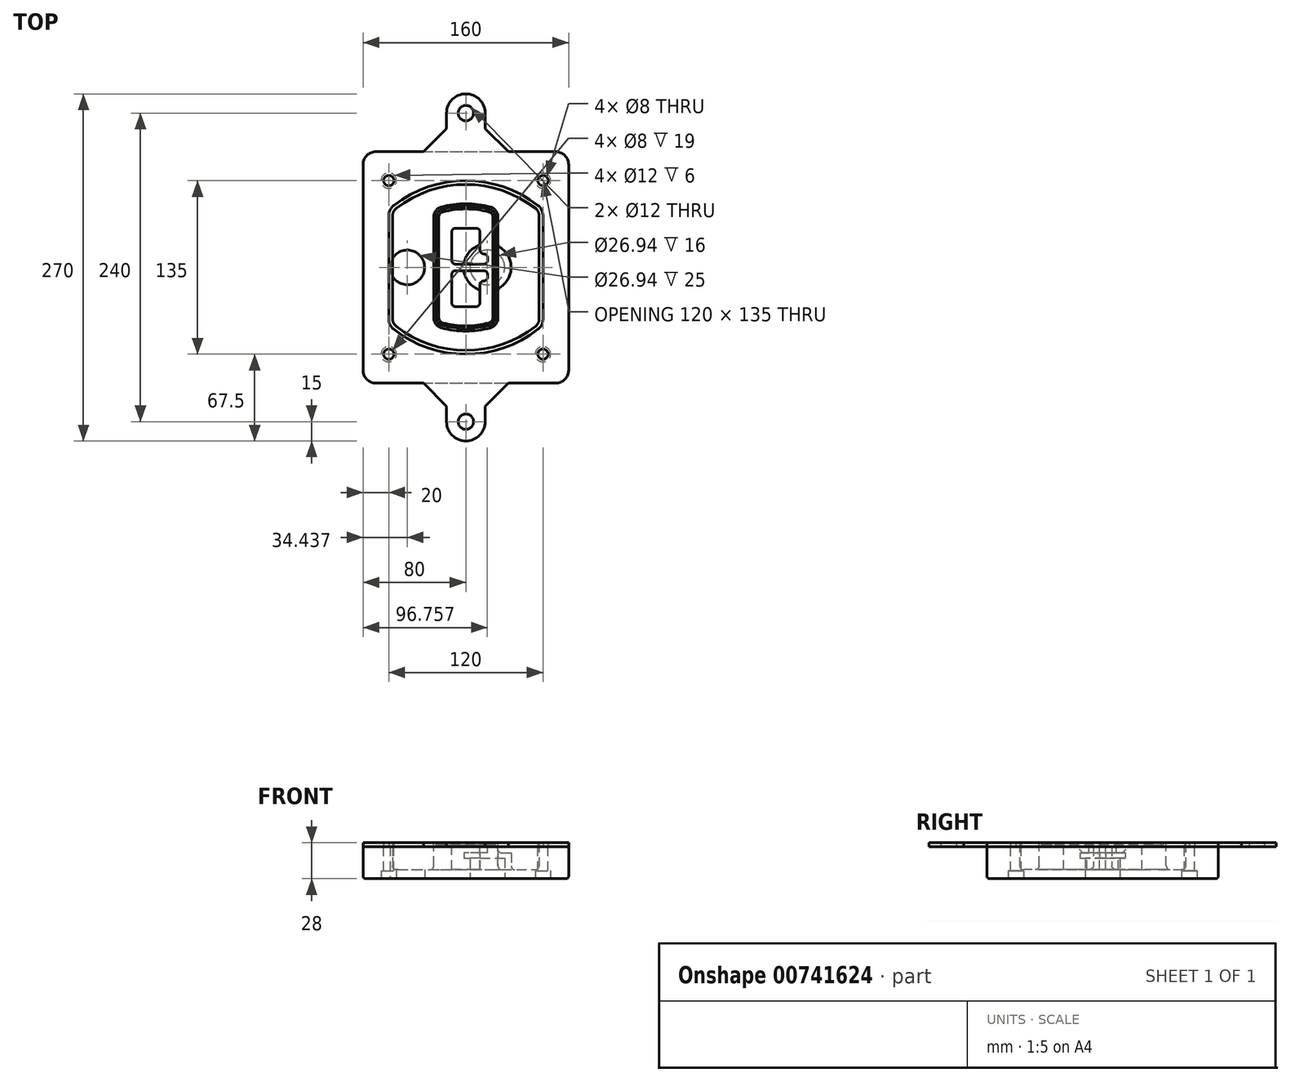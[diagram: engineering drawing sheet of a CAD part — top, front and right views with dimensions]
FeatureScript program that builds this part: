
annotation { "Feature Type Name" : "Feature", "Feature Type Description" : "" }
export const myFeature = defineFeature(function(context is Context, id is Id, definition is map)
    precondition{}
    {
        {
            var Q0;
            Q0=qCreatedBy(makeId("Top.planeOp"),FACE);
            var sketch = newSketch(context, id + "F0", { "sketchPlane" : qUnion([Q0])});
            skPoint(sketch, "E0.rect.middle", {"position": v(0, 0) * mm});
            skLineSegment(sketch, "E1.bottom", {"start": v(-70, -90) * mm, "end": v(70, -90) * mm});
            skLineSegment(sketch, "E1.top", {"start": v(-70, 90) * mm, "end": v(70, 90) * mm});
            skLineSegment(sketch, "E1.left", {"start": v(-80, -80) * mm, "end": v(-80, 80) * mm});
            skLineSegment(sketch, "E1.right", {"start": v(80, -80) * mm, "end": v(80, 80) * mm});
            skLineSegment(sketch, "E2", {"start": v(-80, 90) * mm, "end": v(80, -90) * mm, "construction": true});
            skLineSegment(sketch, "E3", {"start": v(80, 90) * mm, "end": v(-80, -90) * mm, "construction": true});
            skCircle(sketch, "E4", {"center": v(-60, 67.5) * mm, "radius": 4 * mm});
            skCircle(sketch, "E5", {"center": v(60, 67.5) * mm, "radius": 4 * mm});
            skCircle(sketch, "E6", {"center": v(60, -67.5) * mm, "radius": 4 * mm});
            skCircle(sketch, "E7", {"center": v(-60, -67.5) * mm, "radius": 4 * mm});
            skLineSegment(sketch, "E8", {"start": v(-60, 67.5) * mm, "end": v(60, 67.5) * mm, "construction": true});
            skLineSegment(sketch, "E9", {"start": v(60, 67.5) * mm, "end": v(60, -67.5) * mm, "construction": true});
            skLineSegment(sketch, "E10", {"start": v(60, -67.5) * mm, "end": v(-60, -67.5) * mm, "construction": true});
            skLineSegment(sketch, "E11", {"start": v(-60, -67.5) * mm, "end": v(-60, 67.5) * mm, "construction": true});
            skLineSegment(sketch, "E12", {"start": v(-60, 40.3) * mm, "end": v(-60, -40.3) * mm});
            skLineSegment(sketch, "E13", {"start": v(60, 40.3) * mm, "end": v(60, -40.3) * mm});
            skArc(sketch, "E14", {"start": v(56.15, 48.18) * mm, "mid": v(0, 67.5) * mm, "end": v(-56.15, 48.18) * mm});
            skArc(sketch, "E15", {"start": v(-56.15, -48.18) * mm, "mid": v(0, -67.5) * mm, "end": v(56.15, -48.18) * mm});
            skLineSegment(sketch, "E16", {"start": v(-60, 0) * mm, "end": v(60, 0) * mm, "construction": true});
            skPoint(sketch, "E17.visualSharp", {"position": v(-60, -45) * mm});
            skArc(sketch, "E17.filletArc", {"start": v(-60, -40.3) * mm, "mid": v(-58.99, -44.68) * mm, "end": v(-56.15, -48.18) * mm});
            skPoint(sketch, "E18.visualSharp", {"position": v(-60, 45) * mm});
            skArc(sketch, "E18.filletArc", {"start": v(-56.15, 48.18) * mm, "mid": v(-58.99, 44.68) * mm, "end": v(-60, 40.3) * mm});
            skPoint(sketch, "E19.visualSharp", {"position": v(60, 45) * mm});
            skArc(sketch, "E19.filletArc", {"start": v(60, 40.3) * mm, "mid": v(58.99, 44.68) * mm, "end": v(56.15, 48.18) * mm});
            skPoint(sketch, "E20.visualSharp", {"position": v(60, -45) * mm});
            skArc(sketch, "E20.filletArc", {"start": v(56.15, -48.18) * mm, "mid": v(58.99, -44.68) * mm, "end": v(60, -40.3) * mm});
            skPoint(sketch, "E21.visualSharp", {"position": v(-80, 90) * mm});
            skArc(sketch, "E21.filletArc", {"start": v(-70, 90) * mm, "mid": v(-77.07, 87.07) * mm, "end": v(-80, 80) * mm});
            skPoint(sketch, "E22.visualSharp", {"position": v(80, 90) * mm});
            skArc(sketch, "E22.filletArc", {"start": v(80, 80) * mm, "mid": v(77.07, 87.07) * mm, "end": v(70, 90) * mm});
            skPoint(sketch, "E23.visualSharp", {"position": v(80, -90) * mm});
            skArc(sketch, "E23.filletArc", {"start": v(70, -90) * mm, "mid": v(77.07, -87.07) * mm, "end": v(80, -80) * mm});
            skPoint(sketch, "E24.visualSharp", {"position": v(-80, -90) * mm});
            skArc(sketch, "E24.filletArc", {"start": v(-80, -80) * mm, "mid": v(-77.07, -87.07) * mm, "end": v(-70, -90) * mm});
            skArc(sketch, "E25.0", {"start": v(57, 40.3) * mm, "mid": v(56.3, 43.36) * mm, "end": v(54.3, 45.81) * mm});
            skLineSegment(sketch, "E25.1", {"start": v(57, 40.3) * mm, "end": v(57, -40.3) * mm});
            skArc(sketch, "E25.2", {"start": v(54.3, -45.81) * mm, "mid": v(56.3, -43.36) * mm, "end": v(57, -40.3) * mm});
            skArc(sketch, "E25.3", {"start": v(-54.3, -45.81) * mm, "mid": v(0, -64.5) * mm, "end": v(54.3, -45.81) * mm});
            skArc(sketch, "E25.4", {"start": v(-57, -40.3) * mm, "mid": v(-56.3, -43.36) * mm, "end": v(-54.3, -45.81) * mm});
            skArc(sketch, "E25.5", {"start": v(54.3, 45.81) * mm, "mid": v(0, 64.5) * mm, "end": v(-54.3, 45.81) * mm});
            skLineSegment(sketch, "E25.6", {"start": v(-57, 40.3) * mm, "end": v(-57, -40.3) * mm});
            skArc(sketch, "E25.7", {"start": v(-54.3, 45.81) * mm, "mid": v(-56.3, 43.36) * mm, "end": v(-57, 40.3) * mm});
            skArc(sketch, "E26.0", {"start": v(-58.62, 51.33) * mm, "mid": v(-62.58, 46.43) * mm, "end": v(-64, 40.3) * mm});
            skArc(sketch, "E26.1", {"start": v(58.62, 51.33) * mm, "mid": v(0, 71.5) * mm, "end": v(-58.62, 51.33) * mm});
            skArc(sketch, "E26.2", {"start": v(64, 40.3) * mm, "mid": v(62.58, 46.43) * mm, "end": v(58.62, 51.33) * mm});
            skLineSegment(sketch, "E26.3", {"start": v(64, 40.3) * mm, "end": v(64, -40.3) * mm});
            skArc(sketch, "E26.4", {"start": v(58.62, -51.33) * mm, "mid": v(62.58, -46.43) * mm, "end": v(64, -40.3) * mm});
            skLineSegment(sketch, "E26.5", {"start": v(-64, 40.3) * mm, "end": v(-64, -40.3) * mm});
            skArc(sketch, "E26.6", {"start": v(-58.62, -51.33) * mm, "mid": v(0, -71.5) * mm, "end": v(58.62, -51.33) * mm});
            skArc(sketch, "E26.7", {"start": v(-64, -40.3) * mm, "mid": v(-62.58, -46.43) * mm, "end": v(-58.62, -51.33) * mm});
            skSolve(sketch);
        }
        {
            var Q0;
            Q0=makeQuery(id+"F0.imprint","IMPRINT",FACE,{"disambiguationData":[TD([[makeQuery(id+"F0.imprint","IMPRINT",EDGE,{"derivedFrom":sQuery(id+"F0.wireOp",EDGE,"E1.bottom")}),1.0]])]});
            var Q1;
            Q1=makeQuery(id+"F0.imprint","IMPRINT",FACE,{"disambiguationData":[TD([[makeQuery(id+"F0.imprint","IMPRINT",EDGE,{"derivedFrom":sQuery(id+"F0.wireOp",EDGE,"E12")}),1.0]])]});
            var Q2;
            Q2=makeQuery(id+"F0.imprint","IMPRINT",FACE,{"disambiguationData":[TD([[makeQuery(id+"F0.imprint","IMPRINT",EDGE,{"derivedFrom":sQuery(id+"F0.wireOp",EDGE,"E25.0")}),1.0]])]});
            var Q3;
            Q3=makeQuery(id+"F0.imprint","IMPRINT",FACE,{"disambiguationData":[TD([[makeQuery(id+"F0.imprint","IMPRINT",EDGE,{"derivedFrom":sQuery(id+"F0.wireOp",EDGE,"E12")}),-1.0]])]});
            extrude(context, id + "F1", {"entities" : qUnion([Q0, Q1, Q2, Q3]), "oppositeDirection" : true, "depth" : 25 * mm});
        }
        {
            var Q0;
            Q0=makeQuery(id+"F0.imprint","IMPRINT",FACE,{"disambiguationData":[TD([[makeQuery(id+"F0.imprint","IMPRINT",EDGE,{"derivedFrom":sQuery(id+"F0.wireOp",EDGE,"E12")}),1.0]])]});
            extrude(context, id + "F2", {"entities" : qUnion([Q0]), "operationType" : NewBodyOperationType.ADD, "depth" : 3 * mm});
        }
        {
            var Q0;
            Q0=makeQuery(id+"F0.imprint","IMPRINT",FACE,{"disambiguationData":[TD([[makeQuery(id+"F0.imprint","IMPRINT",EDGE,{"derivedFrom":sQuery(id+"F0.wireOp",EDGE,"E25.0")}),1.0]])]});
            extrude(context, id + "F3", {"entities" : qUnion([Q0]), "operationType" : NewBodyOperationType.REMOVE, "oppositeDirection" : true, "depth" : 18 * mm});
        }
        {
            var Q0;
            Q0=makeQuery(id+"F2.opExtrude","CAP_FACE",FACE,{"disambiguationData":[OSD([sQuery(id+"F0.wireOp",EDGE,"E12"),sQuery(id+"F0.wireOp",EDGE,"E13"),sQuery(id+"F0.wireOp",EDGE,"E14"),sQuery(id+"F0.wireOp",EDGE,"E15"),sQuery(id+"F0.wireOp",EDGE,"E17.filletArc"),sQuery(id+"F0.wireOp",EDGE,"E18.filletArc"),sQuery(id+"F0.wireOp",EDGE,"E19.filletArc"),sQuery(id+"F0.wireOp",EDGE,"E20.filletArc"),sQuery(id+"F0.wireOp",EDGE,"E25.0"),sQuery(id+"F0.wireOp",EDGE,"E25.1"),sQuery(id+"F0.wireOp",EDGE,"E25.2"),sQuery(id+"F0.wireOp",EDGE,"E25.3"),sQuery(id+"F0.wireOp",EDGE,"E25.4"),sQuery(id+"F0.wireOp",EDGE,"E25.5"),sQuery(id+"F0.wireOp",EDGE,"E25.6"),sQuery(id+"F0.wireOp",EDGE,"E25.7")])],"isStart":false});
            var sketch = newSketch(context, id + "F4", { "sketchPlane" : qUnion([Q0])});
            skArc(sketch, "E27.0", {"start": v(-19.08, -46.97) * mm, "mid": v(0, -49.5) * mm, "end": v(19.08, -46.97) * mm});
            skArc(sketch, "E28.0", {"start": v(19.08, 46.97) * mm, "mid": v(0, 49.5) * mm, "end": v(-19.08, 46.97) * mm});
            skLineSegment(sketch, "E29", {"start": v(-25, 39.25) * mm, "end": v(-25, -39.25) * mm});
            skLineSegment(sketch, "E30", {"start": v(25, 39.25) * mm, "end": v(25, -39.25) * mm});
            skLineSegment(sketch, "E31", {"start": v(-25, 45.1) * mm, "end": v(25, 45.1) * mm, "construction": true});
            skLineSegment(sketch, "E32", {"start": v(-25, -45.1) * mm, "end": v(25, -45.1) * mm, "construction": true});
            skPoint(sketch, "E33.visualSharp", {"position": v(-25, 45.1) * mm});
            skArc(sketch, "E33.filletArc", {"start": v(-19.08, 46.97) * mm, "mid": v(-23.35, 44.11) * mm, "end": v(-25, 39.25) * mm});
            skPoint(sketch, "E34.visualSharp", {"position": v(25, 45.1) * mm});
            skArc(sketch, "E34.filletArc", {"start": v(25, 39.25) * mm, "mid": v(23.35, 44.11) * mm, "end": v(19.08, 46.97) * mm});
            skPoint(sketch, "E35.visualSharp", {"position": v(25, -45.1) * mm});
            skArc(sketch, "E35.filletArc", {"start": v(19.08, -46.97) * mm, "mid": v(23.35, -44.11) * mm, "end": v(25, -39.25) * mm});
            skPoint(sketch, "E36.visualSharp", {"position": v(-25, -45.1) * mm});
            skArc(sketch, "E36.filletArc", {"start": v(-25, -39.25) * mm, "mid": v(-23.35, -44.11) * mm, "end": v(-19.08, -46.97) * mm});
            skArc(sketch, "E37.0", {"start": v(54.3, 45.81) * mm, "mid": v(0, 64.5) * mm, "end": v(-54.3, 45.81) * mm});
            skArc(sketch, "E37.1", {"start": v(-54.3, 45.81) * mm, "mid": v(-56.3, 43.36) * mm, "end": v(-57, 40.3) * mm});
            skLineSegment(sketch, "E37.2", {"start": v(-57, 40.3) * mm, "end": v(-57, -40.3) * mm});
            skArc(sketch, "E37.3", {"start": v(-57, -40.3) * mm, "mid": v(-56.3, -43.36) * mm, "end": v(-54.3, -45.81) * mm});
            skArc(sketch, "E37.4", {"start": v(-54.3, -45.81) * mm, "mid": v(0, -64.5) * mm, "end": v(54.3, -45.81) * mm});
            skArc(sketch, "E37.5", {"start": v(54.3, -45.81) * mm, "mid": v(56.3, -43.36) * mm, "end": v(57, -40.3) * mm});
            skLineSegment(sketch, "E37.6", {"start": v(57, 40.3) * mm, "end": v(57, -40.3) * mm});
            skArc(sketch, "E37.7", {"start": v(57, 40.3) * mm, "mid": v(56.3, 43.36) * mm, "end": v(54.3, 45.81) * mm});
            skLineSegment(sketch, "E38.0", {"start": v(23, 39.25) * mm, "end": v(23, -39.25) * mm});
            skArc(sketch, "E38.1", {"start": v(18.56, -45.04) * mm, "mid": v(21.76, -42.9) * mm, "end": v(23, -39.25) * mm});
            skArc(sketch, "E38.2", {"start": v(-18.56, -45.04) * mm, "mid": v(0, -47.5) * mm, "end": v(18.56, -45.04) * mm});
            skArc(sketch, "E38.3", {"start": v(-23, -39.25) * mm, "mid": v(-21.76, -42.9) * mm, "end": v(-18.56, -45.04) * mm});
            skLineSegment(sketch, "E38.4", {"start": v(-23, 39.25) * mm, "end": v(-23, -39.25) * mm});
            skArc(sketch, "E38.5", {"start": v(23, 39.25) * mm, "mid": v(21.76, 42.9) * mm, "end": v(18.56, 45.04) * mm});
            skArc(sketch, "E38.6", {"start": v(-18.56, 45.04) * mm, "mid": v(-21.76, 42.9) * mm, "end": v(-23, 39.25) * mm});
            skArc(sketch, "E38.7", {"start": v(18.56, 45.04) * mm, "mid": v(0, 47.5) * mm, "end": v(-18.56, 45.04) * mm});
            skArc(sketch, "E39.0", {"start": v(21, 39.25) * mm, "mid": v(20.18, 41.68) * mm, "end": v(18.04, 43.1) * mm});
            skLineSegment(sketch, "E39.1", {"start": v(21, 39.25) * mm, "end": v(21, -39.25) * mm});
            skArc(sketch, "E39.2", {"start": v(18.04, -43.1) * mm, "mid": v(20.18, -41.68) * mm, "end": v(21, -39.25) * mm});
            skArc(sketch, "E39.3", {"start": v(-18.04, -43.1) * mm, "mid": v(0, -45.5) * mm, "end": v(18.04, -43.1) * mm});
            skArc(sketch, "E39.4", {"start": v(-21, -39.25) * mm, "mid": v(-20.18, -41.68) * mm, "end": v(-18.04, -43.1) * mm});
            skArc(sketch, "E39.5", {"start": v(18.04, 43.1) * mm, "mid": v(0, 45.5) * mm, "end": v(-18.04, 43.1) * mm});
            skLineSegment(sketch, "E39.6", {"start": v(-21, 39.25) * mm, "end": v(-21, -39.25) * mm});
            skArc(sketch, "E39.7", {"start": v(-18.04, 43.1) * mm, "mid": v(-20.18, 41.68) * mm, "end": v(-21, 39.25) * mm});
            skLineSegment(sketch, "E40", {"start": v(-25, 0) * mm, "end": v(25, 0) * mm, "construction": true});
            skLineSegment(sketch, "E41", {"start": v(-11, 5.5) * mm, "end": v(-11, 27.5) * mm});
            skLineSegment(sketch, "E42", {"start": v(-8, 30.5) * mm, "end": v(8, 30.5) * mm});
            skLineSegment(sketch, "E43", {"start": v(11, 27.5) * mm, "end": v(11, 13.5) * mm});
            skLineSegment(sketch, "E44", {"start": v(14, 10.5) * mm, "end": v(14, 10.5) * mm});
            skLineSegment(sketch, "E45", {"start": v(17, 7.5) * mm, "end": v(17, 5.5) * mm});
            skLineSegment(sketch, "E46", {"start": v(14, 2.5) * mm, "end": v(-8, 2.5) * mm});
            skPoint(sketch, "E47.visualSharp", {"position": v(-11, 30.5) * mm});
            skArc(sketch, "E47.filletArc", {"start": v(-8, 30.5) * mm, "mid": v(-10.12, 29.62) * mm, "end": v(-11, 27.5) * mm});
            skPoint(sketch, "E48.visualSharp", {"position": v(11, 30.5) * mm});
            skArc(sketch, "E48.filletArc", {"start": v(11, 27.5) * mm, "mid": v(10.12, 29.62) * mm, "end": v(8, 30.5) * mm});
            skPoint(sketch, "E49.visualSharp", {"position": v(11, 10.5) * mm});
            skArc(sketch, "E49.filletArc", {"start": v(11, 13.5) * mm, "mid": v(11.88, 11.38) * mm, "end": v(14, 10.5) * mm});
            skPoint(sketch, "E50.visualSharp", {"position": v(17, 10.5) * mm});
            skArc(sketch, "E50.filletArc", {"start": v(17, 7.5) * mm, "mid": v(16.12, 9.62) * mm, "end": v(14, 10.5) * mm});
            skPoint(sketch, "E51.visualSharp", {"position": v(17, 2.5) * mm});
            skArc(sketch, "E51.filletArc", {"start": v(14, 2.5) * mm, "mid": v(16.12, 3.38) * mm, "end": v(17, 5.5) * mm});
            skPoint(sketch, "E52.visualSharp", {"position": v(-11, 2.5) * mm});
            skArc(sketch, "E52.filletArc", {"start": v(-11, 5.5) * mm, "mid": v(-10.12, 3.38) * mm, "end": v(-8, 2.5) * mm});
            skLineSegment(sketch, "E53.0.MirrorCS", {"start": v(14, -2.5) * mm, "end": v(-8, -2.5) * mm});
            skArc(sketch, "E54.0.MirrorCS", {"start": v(-11, -5.5) * mm, "mid": v(-10.12, -3.38) * mm, "end": v(-8, -2.5) * mm});
            skLineSegment(sketch, "E55.0.MirrorCS", {"start": v(-11, -5.5) * mm, "end": v(-11, -27.5) * mm});
            skArc(sketch, "E56.0.MirrorCS", {"start": v(-8, -30.5) * mm, "mid": v(-10.12, -29.62) * mm, "end": v(-11, -27.5) * mm});
            skLineSegment(sketch, "E57.0.MirrorCS", {"start": v(-8, -30.5) * mm, "end": v(8, -30.5) * mm});
            skArc(sketch, "E58.0.MirrorCS", {"start": v(11, -27.5) * mm, "mid": v(10.12, -29.62) * mm, "end": v(8, -30.5) * mm});
            skLineSegment(sketch, "E59.0.MirrorCS", {"start": v(11, -27.5) * mm, "end": v(11, -13.5) * mm});
            skArc(sketch, "E60.0.MirrorCS", {"start": v(11, -13.5) * mm, "mid": v(11.88, -11.38) * mm, "end": v(14, -10.5) * mm});
            skArc(sketch, "E61.0.MirrorCS", {"start": v(17, -7.5) * mm, "mid": v(16.12, -9.62) * mm, "end": v(14, -10.5) * mm});
            skLineSegment(sketch, "E62.0.MirrorCS", {"start": v(17, -7.5) * mm, "end": v(17, -5.5) * mm});
            skArc(sketch, "E63.0.MirrorCS", {"start": v(14, -2.5) * mm, "mid": v(16.12, -3.38) * mm, "end": v(17, -5.5) * mm});
            skSolve(sketch);
        }
        {
            var Q0;
            Q0=makeQuery(id+"F4.imprint","IMPRINT",FACE,{"disambiguationData":[TD([[makeQuery(id+"F4.imprint","IMPRINT",EDGE,{"derivedFrom":sQuery(id+"F4.wireOp",EDGE,"E27.0")}),1.0]])]});
            var Q1;
            Q1=makeQuery(id+"F4.imprint","IMPRINT",FACE,{"disambiguationData":[TD([[makeQuery(id+"F4.imprint","IMPRINT",EDGE,{"derivedFrom":sQuery(id+"F4.wireOp",EDGE,"E38.0")}),-1.0]])]});
            var Q2;
            Q2=makeQuery(id+"F4.imprint","IMPRINT",FACE,{"disambiguationData":[TD([[makeQuery(id+"F4.imprint","IMPRINT",EDGE,{"derivedFrom":sQuery(id+"F4.wireOp",EDGE,"E39.0")}),1.0]])]});
            extrude(context, id + "F5", {"entities" : qUnion([Q0, Q1, Q2]), "operationType" : NewBodyOperationType.ADD, "endBound" : BoundingType.UP_TO_NEXT, "oppositeDirection" : true, "depth" : 25 * mm});
        }
        {
            var Q0;
            Q0=makeQuery(id+"F4.imprint","IMPRINT",FACE,{"disambiguationData":[TD([[makeQuery(id+"F4.imprint","IMPRINT",EDGE,{"derivedFrom":sQuery(id+"F4.wireOp",EDGE,"E38.0")}),-1.0]])]});
            extrude(context, id + "F6", {"entities" : qUnion([Q0]), "operationType" : NewBodyOperationType.REMOVE, "oppositeDirection" : true, "depth" : 2 * mm});
        }
        {
            var Q0;
            Q0=makeQuery(id+"F1.opExtrude","CAP_FACE",FACE,{"disambiguationData":[OSD([sQuery(id+"F0.wireOp",EDGE,"E1.bottom"),sQuery(id+"F0.wireOp",EDGE,"E1.top"),sQuery(id+"F0.wireOp",EDGE,"E1.left"),sQuery(id+"F0.wireOp",EDGE,"E1.right"),sQuery(id+"F0.wireOp",EDGE,"E4"),sQuery(id+"F0.wireOp",EDGE,"E5"),sQuery(id+"F0.wireOp",EDGE,"E6"),sQuery(id+"F0.wireOp",EDGE,"E7"),sQuery(id+"F0.wireOp",EDGE,"E21.filletArc"),sQuery(id+"F0.wireOp",EDGE,"E22.filletArc"),sQuery(id+"F0.wireOp",EDGE,"E23.filletArc"),sQuery(id+"F0.wireOp",EDGE,"E24.filletArc")])],"isStart":false});
            var sketch = newSketch(context, id + "F7", { "sketchPlane" : qUnion([Q0])});
            skCircle(sketch, "E64", {"center": v(16.76, 0) * mm, "radius": 13.47 * mm});
            skCircle(sketch, "E65", {"center": v(-45.56, 0) * mm, "radius": 13.47 * mm});
            skLineSegment(sketch, "E66", {"start": v(80, 0) * mm, "end": v(-80, 0) * mm});
            skCircle(sketch, "E67", {"center": v(16.76, 0) * mm, "radius": 18.47 * mm});
            skCircle(sketch, "E68", {"center": v(60, -67.5) * mm, "radius": 6 * mm});
            skCircle(sketch, "E69", {"center": v(-60, -67.5) * mm, "radius": 6 * mm});
            skCircle(sketch, "E70", {"center": v(-60, 67.5) * mm, "radius": 6 * mm});
            skCircle(sketch, "E71", {"center": v(60, 67.5) * mm, "radius": 6 * mm});
            skSolve(sketch);
        }
        {
            var Q0;
            {var subQ1=sQuery(id+"F7.wireOp",EDGE,"E66");var subQ4=sQuery(id+"F7.wireOp",EDGE,"E64");var subQ6=makeQuery(id+"F7.imprint","INTERSECT",VERTEX,{"disambiguationData":[OD(0.0)],"derivedFrom":[subQ4,subQ1]});Q0=makeQuery(id+"F7.imprint","IMPRINT",FACE,{"disambiguationData":[TD([[makeQuery(id+"F7.imprint","IMPRINT",EDGE,{"disambiguationData":[TD([[subQ6,-1.0]])],"derivedFrom":subQ4}),-1.0]])]});}
            var Q1;
            {var subQ0=sQuery(id+"F7.wireOp",EDGE,"E66");var subQ1=sQuery(id+"F7.wireOp",EDGE,"E64");var subQ3=makeQuery(id+"F7.imprint","INTERSECT",VERTEX,{"disambiguationData":[OD(0.0)],"derivedFrom":[subQ1,subQ0]});Q1=makeQuery(id+"F7.imprint","IMPRINT",FACE,{"disambiguationData":[TD([[makeQuery(id+"F7.imprint","IMPRINT",EDGE,{"disambiguationData":[TD([[subQ3,-1.0]])],"derivedFrom":subQ1}),1.0]])]});}
            var Q2;
            {var subQ0=sQuery(id+"F7.wireOp",EDGE,"E66");var subQ1=sQuery(id+"F7.wireOp",EDGE,"E64");var subQ3=makeQuery(id+"F7.imprint","INTERSECT",VERTEX,{"disambiguationData":[OD(0.0)],"derivedFrom":[subQ1,subQ0]});Q2=makeQuery(id+"F7.imprint","IMPRINT",FACE,{"disambiguationData":[TD([[makeQuery(id+"F7.imprint","IMPRINT",EDGE,{"disambiguationData":[TD([[subQ3,1.0]])],"derivedFrom":subQ1}),1.0]])]});}
            var Q3;
            {var subQ1=sQuery(id+"F7.wireOp",EDGE,"E66");var subQ4=sQuery(id+"F7.wireOp",EDGE,"E64");var subQ6=makeQuery(id+"F7.imprint","INTERSECT",VERTEX,{"disambiguationData":[OD(0.0)],"derivedFrom":[subQ4,subQ1]});Q3=makeQuery(id+"F7.imprint","IMPRINT",FACE,{"disambiguationData":[TD([[makeQuery(id+"F7.imprint","IMPRINT",EDGE,{"disambiguationData":[TD([[subQ6,1.0]])],"derivedFrom":subQ4}),-1.0]])]});}
            extrude(context, id + "F8", {"entities" : qUnion([Q0, Q1, Q2, Q3]), "operationType" : NewBodyOperationType.ADD, "oppositeDirection" : true, "depth" : 20 * mm});
        }
        {
            var Q0;
            {var subQ0=sQuery(id+"F7.wireOp",EDGE,"E66");var subQ1=sQuery(id+"F7.wireOp",EDGE,"E64");var subQ3=makeQuery(id+"F7.imprint","INTERSECT",VERTEX,{"disambiguationData":[OD(0.0)],"derivedFrom":[subQ1,subQ0]});Q0=makeQuery(id+"F7.imprint","IMPRINT",FACE,{"disambiguationData":[TD([[makeQuery(id+"F7.imprint","IMPRINT",EDGE,{"disambiguationData":[TD([[subQ3,-1.0]])],"derivedFrom":subQ1}),1.0]])]});}
            var Q1;
            {var subQ0=sQuery(id+"F7.wireOp",EDGE,"E66");var subQ1=sQuery(id+"F7.wireOp",EDGE,"E64");var subQ3=makeQuery(id+"F7.imprint","INTERSECT",VERTEX,{"disambiguationData":[OD(0.0)],"derivedFrom":[subQ1,subQ0]});Q1=makeQuery(id+"F7.imprint","IMPRINT",FACE,{"disambiguationData":[TD([[makeQuery(id+"F7.imprint","IMPRINT",EDGE,{"disambiguationData":[TD([[subQ3,1.0]])],"derivedFrom":subQ1}),1.0]])]});}
            extrude(context, id + "F9", {"entities" : qUnion([Q0, Q1]), "operationType" : NewBodyOperationType.REMOVE, "oppositeDirection" : true, "depth" : 16 * mm});
        }
        {
            var Q0;
            {var subQ0=sQuery(id+"F7.wireOp",EDGE,"E66");var subQ1=sQuery(id+"F7.wireOp",EDGE,"E65");var subQ3=makeQuery(id+"F7.imprint","INTERSECT",VERTEX,{"disambiguationData":[OD(0.0)],"derivedFrom":[subQ1,subQ0]});Q0=makeQuery(id+"F7.imprint","IMPRINT",FACE,{"disambiguationData":[TD([[makeQuery(id+"F7.imprint","IMPRINT",EDGE,{"disambiguationData":[TD([[subQ3,-1.0]])],"derivedFrom":subQ1}),1.0]])]});}
            var Q1;
            {var subQ0=sQuery(id+"F7.wireOp",EDGE,"E66");var subQ1=sQuery(id+"F7.wireOp",EDGE,"E65");var subQ3=makeQuery(id+"F7.imprint","INTERSECT",VERTEX,{"disambiguationData":[OD(0.0)],"derivedFrom":[subQ1,subQ0]});Q1=makeQuery(id+"F7.imprint","IMPRINT",FACE,{"disambiguationData":[TD([[makeQuery(id+"F7.imprint","IMPRINT",EDGE,{"disambiguationData":[TD([[subQ3,1.0]])],"derivedFrom":subQ1}),1.0]])]});}
            extrude(context, id + "F10", {"entities" : qUnion([Q0, Q1]), "operationType" : NewBodyOperationType.REMOVE, "oppositeDirection" : true, "depth" : 25 * mm});
        }
        {
            var Q0;
            Q0=makeQuery(id+"F7.imprint","IMPRINT",FACE,{"disambiguationData":[TD([[makeQuery(id+"F7.imprint","IMPRINT",EDGE,{"derivedFrom":sQuery(id+"F7.wireOp",EDGE,"E68")}),1.0]])]});
            var Q1;
            Q1=makeQuery(id+"F7.imprint","IMPRINT",FACE,{"disambiguationData":[TD([[makeQuery(id+"F7.imprint","IMPRINT",EDGE,{"derivedFrom":makeQuery(id+"F1.opExtrude","CAP_EDGE",EDGE,{"disambiguationData":[OSD([sQuery(id+"F0.wireOp",EDGE,"E5")])],"isStart":false})}),-1.0]])]});
            var Q2;
            Q2=makeQuery(id+"F7.imprint","IMPRINT",FACE,{"disambiguationData":[TD([[makeQuery(id+"F7.imprint","IMPRINT",EDGE,{"derivedFrom":sQuery(id+"F7.wireOp",EDGE,"E69")}),1.0]])]});
            var Q3;
            Q3=makeQuery(id+"F7.imprint","IMPRINT",FACE,{"disambiguationData":[TD([[makeQuery(id+"F7.imprint","IMPRINT",EDGE,{"derivedFrom":makeQuery(id+"F1.opExtrude","CAP_EDGE",EDGE,{"disambiguationData":[OSD([sQuery(id+"F0.wireOp",EDGE,"E4")])],"isStart":false})}),-1.0]])]});
            var Q4;
            Q4=makeQuery(id+"F7.imprint","IMPRINT",FACE,{"disambiguationData":[TD([[makeQuery(id+"F7.imprint","IMPRINT",EDGE,{"derivedFrom":sQuery(id+"F7.wireOp",EDGE,"E70")}),1.0]])]});
            var Q5;
            Q5=makeQuery(id+"F7.imprint","IMPRINT",FACE,{"disambiguationData":[TD([[makeQuery(id+"F7.imprint","IMPRINT",EDGE,{"derivedFrom":makeQuery(id+"F1.opExtrude","CAP_EDGE",EDGE,{"disambiguationData":[OSD([sQuery(id+"F0.wireOp",EDGE,"E7")])],"isStart":false})}),-1.0]])]});
            var Q6;
            Q6=makeQuery(id+"F7.imprint","IMPRINT",FACE,{"disambiguationData":[TD([[makeQuery(id+"F7.imprint","IMPRINT",EDGE,{"derivedFrom":sQuery(id+"F7.wireOp",EDGE,"E71")}),1.0]])]});
            var Q7;
            Q7=makeQuery(id+"F7.imprint","IMPRINT",FACE,{"disambiguationData":[TD([[makeQuery(id+"F7.imprint","IMPRINT",EDGE,{"derivedFrom":makeQuery(id+"F1.opExtrude","CAP_EDGE",EDGE,{"disambiguationData":[OSD([sQuery(id+"F0.wireOp",EDGE,"E6")])],"isStart":false})}),-1.0]])]});
            extrude(context, id + "F11", {"entities" : qUnion([Q0, Q1, Q2, Q3, Q4, Q5, Q6, Q7]), "operationType" : NewBodyOperationType.REMOVE, "oppositeDirection" : true, "depth" : 6 * mm});
        }
        {
            var Q0;
            Q0=makeQuery(id+"F9.boolean.opBoolean","COPY",FACE,{"derivedFrom":makeQuery(id+"F9.opExtrude","CAP_FACE",FACE,{"disambiguationData":[OSD([sQuery(id+"F7.wireOp",EDGE,"E64")])],"isStart":false})});
            var sketch = newSketch(context, id + "F12", { "sketchPlane" : qUnion([Q0])});
            skArc(sketch, "E72.0", {"start": v(11, 17.55) * mm, "mid": v(2.57, 11.82) * mm, "end": v(-1.54, 2.5) * mm});
            skArc(sketch, "E72.1", {"start": v(-1.54, -2.5) * mm, "mid": v(2.57, -11.82) * mm, "end": v(11, -17.55) * mm});
            skLineSegment(sketch, "E73", {"start": v(-1.54, -2.5) * mm, "end": v(14, -2.5) * mm});
            skLineSegment(sketch, "E74.0", {"start": v(14, 2.5) * mm, "end": v(-1.54, 2.5) * mm});
            skArc(sketch, "E74.1", {"start": v(14, 2.5) * mm, "mid": v(16.12, 3.38) * mm, "end": v(17, 5.5) * mm});
            skLineSegment(sketch, "E74.2", {"start": v(17, 7.5) * mm, "end": v(17, 5.5) * mm});
            skArc(sketch, "E74.3", {"start": v(17, 7.5) * mm, "mid": v(16.12, 9.62) * mm, "end": v(14, 10.5) * mm});
            skArc(sketch, "E74.4", {"start": v(11, 13.5) * mm, "mid": v(11.88, 11.38) * mm, "end": v(14, 10.5) * mm});
            skLineSegment(sketch, "E74.5", {"start": v(11, 17.55) * mm, "end": v(11, 13.5) * mm});
            skLineSegment(sketch, "E74.7", {"start": v(14, -2.5) * mm, "end": v(-1.54, -2.5) * mm});
            skArc(sketch, "E74.8", {"start": v(14, -2.5) * mm, "mid": v(16.12, -3.38) * mm, "end": v(17, -5.5) * mm});
            skLineSegment(sketch, "E74.9", {"start": v(17, -7.5) * mm, "end": v(17, -5.5) * mm});
            skArc(sketch, "E74.10", {"start": v(17, -7.5) * mm, "mid": v(16.12, -9.62) * mm, "end": v(14, -10.5) * mm});
            skArc(sketch, "E74.11", {"start": v(11, -13.5) * mm, "mid": v(11.88, -11.38) * mm, "end": v(14, -10.5) * mm});
            skLineSegment(sketch, "E74.12", {"start": v(11, -17.55) * mm, "end": v(11, -13.5) * mm});
            skPoint(sketch, "E75.orphan", {"position": v(11, -27.5) * mm});
            skPoint(sketch, "E76.orphan", {"position": v(-8, -2.5) * mm});
            skPoint(sketch, "E77.orphan", {"position": v(-8, 2.5) * mm});
            skPoint(sketch, "E78.orphan", {"position": v(11, 27.5) * mm});
            skSolve(sketch);
        }
        {
            var Q0;
            {var subQ7=sQuery(id+"F12.wireOp",EDGE,"E72.0");var subQ14=sQuery(id+"F12.wireOp",EDGE,"E72.1");var subQ16=sQuery(id+"F12.wireOp",EDGE,"E74.1");var subQ18=sQuery(id+"F12.wireOp",EDGE,"E74.8");Q0=qUnion([makeQuery(id+"F12.imprint","IMPRINT",FACE,{"disambiguationData":[TD([[makeQuery(id+"F12.imprint","IMPRINT",EDGE,{"derivedFrom":subQ7}),1.0]])]}),makeQuery(id+"F12.imprint","IMPRINT",FACE,{"disambiguationData":[TD([[makeQuery(id+"F12.imprint","IMPRINT",EDGE,{"derivedFrom":subQ14}),1.0]])]}),makeQuery(id+"F12.imprint","IMPRINT",FACE,{"disambiguationData":[TD([[makeQuery(id+"F12.imprint","IMPRINT",EDGE,{"derivedFrom":subQ16}),1.0]])]}),makeQuery(id+"F12.imprint","IMPRINT",FACE,{"disambiguationData":[TD([[makeQuery(id+"F12.imprint","IMPRINT",EDGE,{"derivedFrom":subQ18}),-1.0]])]})]);}
            var Q1;
            Q1=makeQuery(id+"F5.boolean.opBoolean","SPLIT",FACE,{"disambiguationData":[TD([makeQuery(id+"F5.opExtrude","SWEPT_FACE",FACE,{"disambiguationData":[OSD([sQuery(id+"F4.wireOp",EDGE,"E41")])]})])],"derivedFrom":makeQuery(id+"F3.boolean.opBoolean","COPY",FACE,{"derivedFrom":makeQuery(id+"F3.opExtrude","CAP_FACE",FACE,{"disambiguationData":[OSD([sQuery(id+"F0.wireOp",EDGE,"E25.0"),sQuery(id+"F0.wireOp",EDGE,"E25.1"),sQuery(id+"F0.wireOp",EDGE,"E25.2"),sQuery(id+"F0.wireOp",EDGE,"E25.3"),sQuery(id+"F0.wireOp",EDGE,"E25.4"),sQuery(id+"F0.wireOp",EDGE,"E25.5"),sQuery(id+"F0.wireOp",EDGE,"E25.6"),sQuery(id+"F0.wireOp",EDGE,"E25.7")])],"isStart":false})})});
            extrude(context, id + "F13", {"entities" : qUnion([Q0]), "operationType" : NewBodyOperationType.REMOVE, "endBound" : BoundingType.UP_TO_SURFACE, "endBoundEntityFace" : qUnion([Q1]), "depth" : 25 * mm});
        }
        {
            var Q0;
            Q0=makeQuery(id+"F3.boolean.opBoolean","COPY",EDGE,{"derivedFrom":makeQuery(id+"F3.opExtrude","CAP_EDGE",EDGE,{"disambiguationData":[OSD([sQuery(id+"F0.wireOp",EDGE,"E25.6")])],"isStart":false})});
            var Q1;
            Q1=makeQuery(id+"F8.boolean.opBoolean","INTERSECT",EDGE,{"derivedFrom":[makeQuery(id+"F5.opExtrude","SWEPT_FACE",FACE,{"disambiguationData":[OSD([sQuery(id+"F4.wireOp",EDGE,"E30")])]}),makeQuery(id+"F8.opExtrude","CAP_FACE",FACE,{"disambiguationData":[OSD([sQuery(id+"F7.wireOp",EDGE,"E67")])],"isStart":false})]});
            var Q2;
            Q2=makeQuery(id+"F8.boolean.opBoolean","INTERSECT",EDGE,{"disambiguationData":[OD(1.0)],"derivedFrom":[makeQuery(id+"F5.opExtrude","SWEPT_FACE",FACE,{"disambiguationData":[OSD([sQuery(id+"F4.wireOp",EDGE,"E30")])]}),makeQuery(id+"F8.opExtrude","SWEPT_FACE",FACE,{"disambiguationData":[OSD([sQuery(id+"F7.wireOp",EDGE,"E67")])]})]});
            var Q3;
            {var subQ0=sQuery(id+"F4.wireOp",EDGE,"E30");Q3=makeQuery(id+"F8.boolean.opBoolean","SPLIT",EDGE,{"disambiguationData":[TD([makeQuery(id+"F5.opExtrude","SWEPT_FACE",FACE,{"disambiguationData":[OSD([sQuery(id+"F4.wireOp",EDGE,"E35.filletArc")])]})])],"derivedFrom":makeQuery(id+"F5.opExtrude","CAP_EDGE",EDGE,{"disambiguationData":[OSD([subQ0])],"isStart":false})});}
            var Q4;
            {var subQ0=sQuery(id+"F0.wireOp",EDGE,"E25.7");var subQ1=sQuery(id+"F0.wireOp",EDGE,"E25.1");var subQ2=sQuery(id+"F0.wireOp",EDGE,"E25.6");var subQ3=sQuery(id+"F0.wireOp",EDGE,"E25.5");var subQ4=sQuery(id+"F0.wireOp",EDGE,"E25.4");var subQ5=sQuery(id+"F0.wireOp",EDGE,"E25.0");var subQ6=sQuery(id+"F0.wireOp",EDGE,"E25.2");var subQ7=sQuery(id+"F0.wireOp",EDGE,"E25.3");Q4=makeQuery(id+"F8.boolean.opBoolean","INTERSECT",EDGE,{"derivedFrom":[makeQuery(id+"F5.boolean.opBoolean","SPLIT",FACE,{"disambiguationData":[TD([makeQuery(id+"F2.opExtrude","SWEPT_FACE",FACE,{"disambiguationData":[OSD([subQ5])]})])],"derivedFrom":makeQuery(id+"F3.boolean.opBoolean","COPY",FACE,{"derivedFrom":makeQuery(id+"F3.opExtrude","CAP_FACE",FACE,{"disambiguationData":[OSD([subQ5,subQ1,subQ6,subQ7,subQ4,subQ3,subQ2,subQ0])],"isStart":false})})}),makeQuery(id+"F8.opExtrude","SWEPT_FACE",FACE,{"disambiguationData":[OSD([sQuery(id+"F7.wireOp",EDGE,"E67")])]})]});}
            var Q5;
            Q5=makeQuery(id+"F8.boolean.opBoolean","INTERSECT",EDGE,{"disambiguationData":[OD(0.0)],"derivedFrom":[makeQuery(id+"F5.opExtrude","SWEPT_FACE",FACE,{"disambiguationData":[OSD([sQuery(id+"F4.wireOp",EDGE,"E30")])]}),makeQuery(id+"F8.opExtrude","SWEPT_FACE",FACE,{"disambiguationData":[OSD([sQuery(id+"F7.wireOp",EDGE,"E67")])]})]});
            fillet(context, id + "F14", {"entities" : qUnion([Q0, Q1, Q2, Q3, Q4, Q5]), "radius" : 3 * mm, "tangentPropagation" : true, "allowEdgeOverflow" : false});
        }
        {
            var Q0;
            Q0=makeQuery(id+"F1.opExtrude","CAP_EDGE",EDGE,{"disambiguationData":[OSD([sQuery(id+"F0.wireOp",EDGE,"E1.bottom")])],"isStart":false});
            fillet(context, id + "F15", {"entities" : qUnion([Q0]), "radius" : 2 * mm, "tangentPropagation" : true, "allowEdgeOverflow" : false});
        }
        {
            var Q0;
            {var subQ0=sQuery(id+"F0.wireOp",EDGE,"E21.filletArc");var subQ1=sQuery(id+"F0.wireOp",EDGE,"E7");var subQ2=sQuery(id+"F0.wireOp",EDGE,"E6");var subQ3=sQuery(id+"F0.wireOp",EDGE,"E5");var subQ4=sQuery(id+"F0.wireOp",EDGE,"E4");var subQ5=sQuery(id+"F0.wireOp",EDGE,"E22.filletArc");var subQ6=sQuery(id+"F0.wireOp",EDGE,"E1.bottom");var subQ7=sQuery(id+"F0.wireOp",EDGE,"E1.right");var subQ8=sQuery(id+"F0.wireOp",EDGE,"E1.top");var subQ9=sQuery(id+"F0.wireOp",EDGE,"E1.left");var subQ10=sQuery(id+"F0.wireOp",EDGE,"E23.filletArc");var subQ11=sQuery(id+"F0.wireOp",EDGE,"E24.filletArc");Q0=makeQuery(id+"F2.boolean.opBoolean","SPLIT",FACE,{"disambiguationData":[TD([makeQuery(id+"F1.opExtrude","SWEPT_FACE",FACE,{"disambiguationData":[OSD([subQ6])]})])],"derivedFrom":makeQuery(id+"F1.opExtrude","CAP_FACE",FACE,{"disambiguationData":[OSD([subQ6,subQ8,subQ9,subQ7,subQ4,subQ3,subQ2,subQ1,subQ0,subQ5,subQ10,subQ11])],"isStart":true})});}
            var sketch = newSketch(context, id + "F16", { "sketchPlane" : qUnion([Q0])});
            skLineSegment(sketch, "E79", {"start": v(0, 90) * mm, "end": v(0, 120) * mm, "construction": true});
            skCircle(sketch, "E80", {"center": v(0, 120) * mm, "radius": 6 * mm});
            skLineSegment(sketch, "E81", {"start": v(-33, 90) * mm, "end": v(-15, 108) * mm});
            skLineSegment(sketch, "E82", {"start": v(33, 90) * mm, "end": v(15, 108) * mm});
            skLineSegment(sketch, "E83", {"start": v(-15, 108) * mm, "end": v(-15, 120) * mm});
            skLineSegment(sketch, "E84", {"start": v(15, 108) * mm, "end": v(15, 120) * mm});
            skArc(sketch, "E85", {"start": v(15, 120) * mm, "mid": v(0, 135) * mm, "end": v(-15, 120) * mm});
            skLineSegment(sketch, "E86", {"start": v(-80, 0) * mm, "end": v(80, 0) * mm, "construction": true});
            skLineSegment(sketch, "E87.MirrorCS", {"start": v(-33, -90) * mm, "end": v(-15, -108) * mm});
            skLineSegment(sketch, "E88.MirrorCS", {"start": v(-15, -108) * mm, "end": v(-15, -120) * mm});
            skArc(sketch, "E89.MirrorCS", {"start": v(15, -120) * mm, "mid": v(0, -135) * mm, "end": v(-15, -120) * mm});
            skCircle(sketch, "E90.MirrorC", {"center": v(0, -120) * mm, "radius": 6 * mm});
            skLineSegment(sketch, "E91.MirrorCS", {"start": v(0, -90) * mm, "end": v(0, -120) * mm, "construction": true});
            skLineSegment(sketch, "E92.MirrorCS", {"start": v(15, -108) * mm, "end": v(15, -120) * mm});
            skLineSegment(sketch, "E93.MirrorCS", {"start": v(33, -90) * mm, "end": v(15, -108) * mm});
            skSolve(sketch);
        }
        {
            var Q0;
            Q0=makeQuery(id+"F16.imprint","IMPRINT",FACE,{"disambiguationData":[TD([[makeQuery(id+"F16.imprint","IMPRINT",EDGE,{"derivedFrom":sQuery(id+"F16.wireOp",EDGE,"E80")}),-1.0]])]});
            var Q1;
            {var subQ0=sQuery(id+"F16.wireOp",EDGE,"E87.MirrorCS");Q1=makeQuery(id+"F16.imprint","IMPRINT",FACE,{"disambiguationData":[TD([[makeQuery(id+"F16.imprint","IMPRINT",EDGE,{"derivedFrom":subQ0}),1.0]])]});}
            var Q2;
            Q2=makeQuery(id+"F16.imprint","IMPRINT",FACE,{"disambiguationData":[TD([[makeQuery(id+"F16.imprint","IMPRINT",EDGE,{"derivedFrom":makeQuery(id+"F1.opExtrude","CAP_EDGE",EDGE,{"disambiguationData":[OSD([sQuery(id+"F0.wireOp",EDGE,"E1.left")])],"isStart":true})}),-1.0]])]});
            var Q3;
            Q3=makeQuery(id+"F2.opExtrude","CAP_FACE",FACE,{"disambiguationData":[OSD([sQuery(id+"F0.wireOp",EDGE,"E12"),sQuery(id+"F0.wireOp",EDGE,"E13"),sQuery(id+"F0.wireOp",EDGE,"E14"),sQuery(id+"F0.wireOp",EDGE,"E15"),sQuery(id+"F0.wireOp",EDGE,"E17.filletArc"),sQuery(id+"F0.wireOp",EDGE,"E18.filletArc"),sQuery(id+"F0.wireOp",EDGE,"E19.filletArc"),sQuery(id+"F0.wireOp",EDGE,"E20.filletArc"),sQuery(id+"F0.wireOp",EDGE,"E25.0"),sQuery(id+"F0.wireOp",EDGE,"E25.1"),sQuery(id+"F0.wireOp",EDGE,"E25.2"),sQuery(id+"F0.wireOp",EDGE,"E25.3"),sQuery(id+"F0.wireOp",EDGE,"E25.4"),sQuery(id+"F0.wireOp",EDGE,"E25.5"),sQuery(id+"F0.wireOp",EDGE,"E25.6"),sQuery(id+"F0.wireOp",EDGE,"E25.7")])],"isStart":false});
            extrude(context, id + "F17", {"entities" : qUnion([Q0, Q1, Q2]), "endBound" : BoundingType.UP_TO_SURFACE, "depth" : 25 * mm, "endBoundEntityFace" : qUnion([Q3]), "offsetDistance" : 25 * mm});
        }
    });
